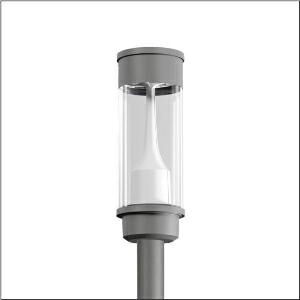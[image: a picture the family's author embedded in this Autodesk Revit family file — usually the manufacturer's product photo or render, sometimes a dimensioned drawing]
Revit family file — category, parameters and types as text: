
# Revit family: litepole_iq___st1_2a_5xa5415mf14h_d5a4
name_source: partatom
category: Lighting Fixtures
units: mm (PartAtom-declared; Revit-internal decimal feet)

## family parameters
Cut with Voids When Loaded = No
Host = Face
Light Source = No
Part Type = Normal
Room Calculation Point = No
Round Connector Dimension = Use Diameter
Shared = No

## types (1)
- --- (1 x LED, 1540 lm, 11.8 W, 2700K)
    Apparent Load = 12 VA
    CIE Flux Codes = 22 61 93 96 100
    Color Rendering = 70
    Color Temperature = 2700K
    Default Elevation = 1800 mm
    Description = Litepole iQ, mast luminaire, Module 540 iQ-SR, primary light control with 3 zone facetted reflector, of plastic, silver coated, highly specular, structured, primary optical cover: cover, of PMMA, transparent, partly coated, light distribution: ST1.2a, light emission: direct distribution, primary light characteristic: asymmetric, installation type: post-top, LED, High Power LED, rated luminous flux: 1.540lm, luminous efficacy: 131lm/W, light colour: 727, colour temperature: 2700K, control gear: ECG iQ, control: optimised constant luminous flux control (CLO 2.0), Desk-Remote (wireless, voltage-free reading and setting of iQ features in the workshop via application-optimized NFC function/RFID function), Light-Fading, Smart-Wire, Night-Set, Lumen-Switch, Temp-Guard, Auto-Match, Street-Remote, presetting dimming logarithmic, with terminal, 6-pole, max. 2.5mm², mains connection: 230..240V, AC, 50/60Hz, start of lifetime: 12W, end of service life: 12W, reduction: 6W, luminaire housing, upper part, of glass-fibre reinforced polyester, coated, Siteco® metallic grey (DB 702S), diameter: 210mm, height: 590mm, spigot size: d x l = 76 x 70mm (post-top) | with reducer (optional accessory) 60 x 70mm, post-top mast mounting element, of diecast aluminium, coated, Siteco® metallic grey (DB 702S), Module 540 iQ-SR, traffic white (RAL 9016), equipment: standard, protection rating (complete): IP65, insulation class (complete): insulation class II (safety insulation), certification: CE, ENEC, VDE, packaging unit: 1 piece

Light Distribution: ST1.2a
    Height = 590 mm
    Lamp = 1 x LED
    Lamp Light Flux = 1540 lm
    Lamp Power = 11.8 W
    Lamp count = 1
    Length = 220 mm
    Luminous efficacy = 131 lm/W
    Manufacturer = Siteco
    ModVariant = No
    Model = 5XA5415MF14H
    Number of Poles = 1
    OnlyDefault = Yes
    Power Factor = 1
    Product Name = Litepole iQ | ST1.2a
    Product group = mast luminaire | pylon top
    ProductGroupID = 6100
    Protection Class = Protection class II
    Protection Degree = IP 65
    RLX_Detail_Level = 1
    RLX_Emergency_Light_Flux = 0 lm
    RLX_Emergency_Type = 0
    RLX_Emergency_Type_DB = No
    RlxData = <blob elided: 71973 chars, md5=6171a8af>
    Socket = socket
    Standby Power = 0 W
    System Light Flux = 1540 lm
    System Power = 12 W
    Type Comments = factory setting: luminous flux: 100 % | dim-lin: 254 | 472 mA
    Type Image = l_1006025.jpg
    URL = http://relux.com
    VarID = @adj_103179
    Voltage = 0 V
    Weight = 0.00 kg
    Width = 0 mm  [stored 0 ft]

note: [stored X ft] marks values corroborated as IEEE doubles in the binary element streams (Revit-internal decimal feet)

## geometry (parser evidence)
native form markers: Blend x4, Sweep x8
no freeform markers — native parametric forms only
